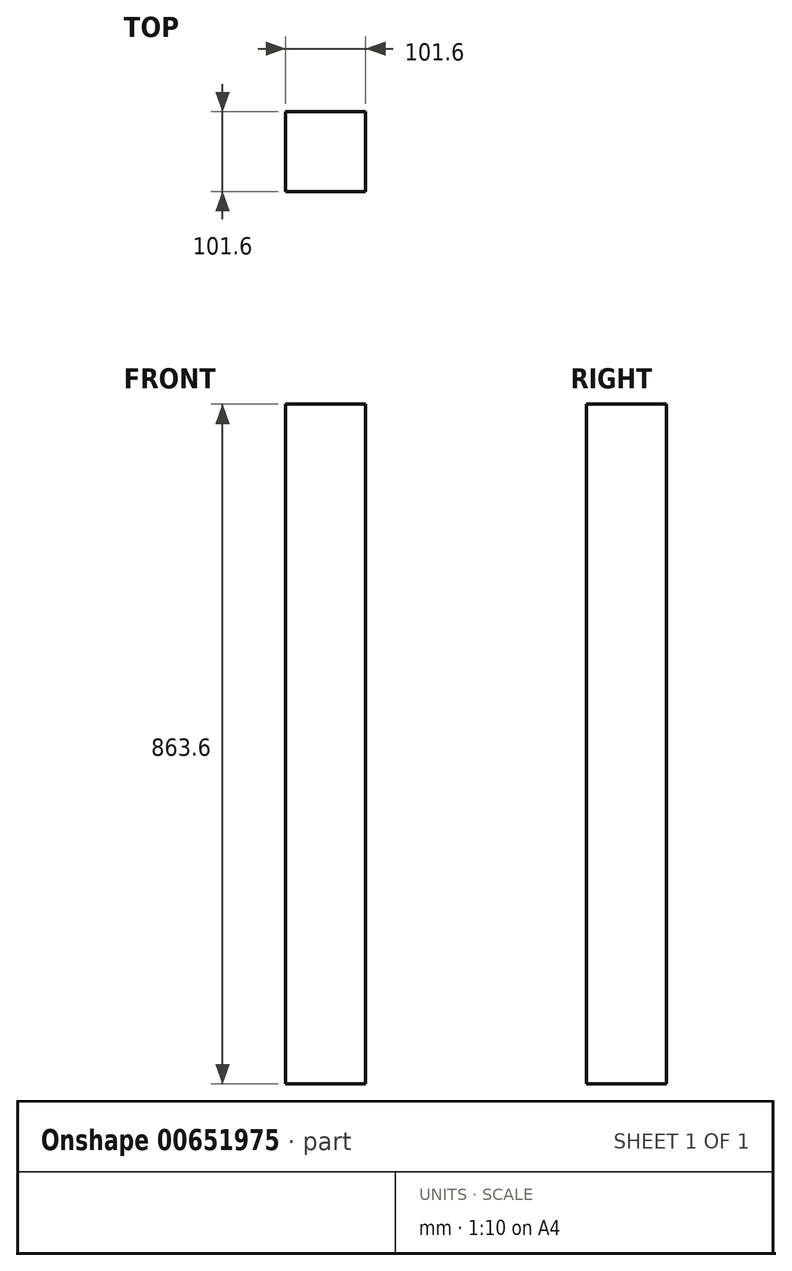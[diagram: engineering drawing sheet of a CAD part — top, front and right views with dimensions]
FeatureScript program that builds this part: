
annotation { "Feature Type Name" : "Feature", "Feature Type Description" : "" }
export const myFeature = defineFeature(function(context is Context, id is Id, definition is map)
    precondition{}
    {
        {
            var Q0;
            Q0=qCreatedBy(makeId("Top.planeOp"),FACE);
            var sketch = newSketch(context, id + "F0", { "sketchPlane" : qUnion([Q0])});
            skLineSegment(sketch, "E0.bottom", {"start": v(0, 0) * mm, "end": v(101.6, 0) * mm});
            skLineSegment(sketch, "E0.top", {"start": v(0, 101.6) * mm, "end": v(101.6, 101.6) * mm});
            skLineSegment(sketch, "E0.left", {"start": v(0, 0) * mm, "end": v(0, 101.6) * mm});
            skLineSegment(sketch, "E0.right", {"start": v(101.6, 0) * mm, "end": v(101.6, 101.6) * mm});
            skSolve(sketch);
        }
        {
            var Q0;
            Q0=makeQuery(id+"F0.imprint","IMPRINT",FACE,{"disambiguationData":[TD([[makeQuery(id+"F0.imprint","IMPRINT",EDGE,{"derivedFrom":sQuery(id+"F0.wireOp",EDGE,"E0.bottom")}),1.0]])]});
            extrude(context, id + "F1", {"entities" : qUnion([Q0]), "depth" : 863.6 * mm, "offsetDistance" : 25.4 * mm});
        }
    });
